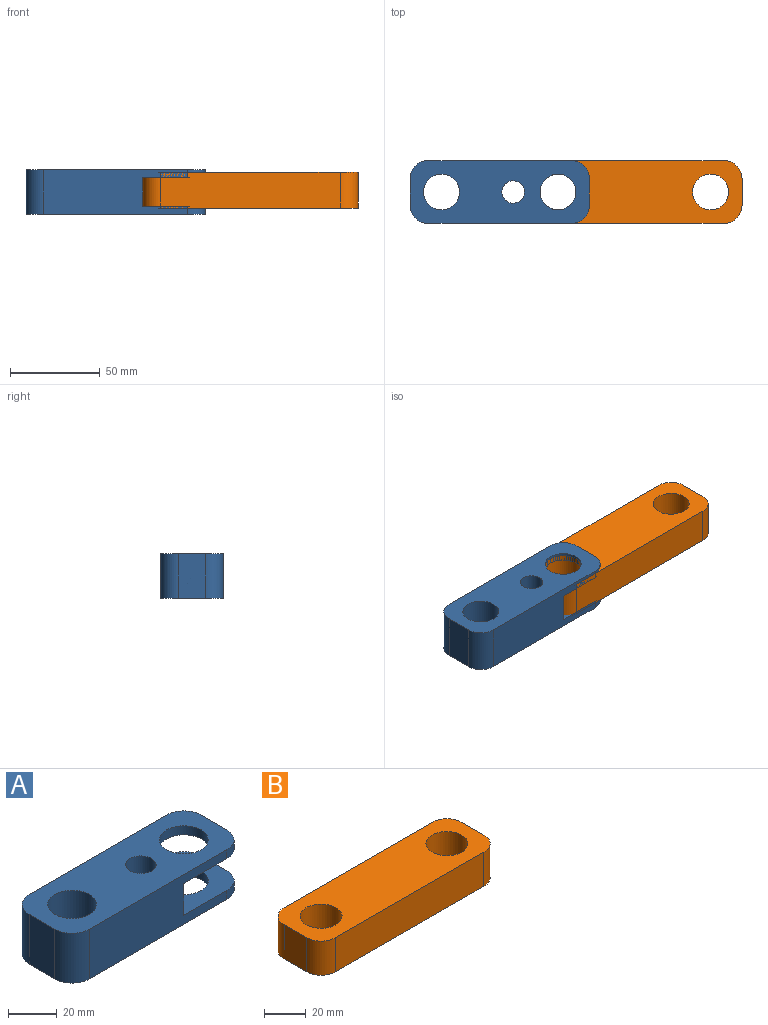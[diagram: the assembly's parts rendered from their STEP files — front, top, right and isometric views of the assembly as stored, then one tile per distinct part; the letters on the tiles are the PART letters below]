
ASSEMBLY  parts=2 mates=1
PART A: 20 faces, bbox 100x35x25 mm
  f0: plane 15x4.5mm, normal (1,0,0), area 67.5mm2, adj f2,f3,f15,f18
  f1: plane 80x25mm, normal (0,-1,0), area 1600mm2, adj f2,f7,f8,f15,f16,f17,f18,f19
  f2: cylinder r=10mm len=10mm, axis (0,0,-1), area 70.7mm2, adj f0,f1,f15,f18
  f3: cylinder r=10mm len=10mm, axis (0,0,-1), area 70.7mm2, adj f0,f4,f15,f18
  f4: plane 80x25mm, normal (0,1,0), area 1600mm2, adj f3,f10,f14,f15,f16,f17,f18,f19
  f5: cylinder r=10mm len=20mm, axis (0,0,-1), area 282.7mm2, adj f15,f18
  f6: plane 25x15mm, normal (-1,0,0), area 375mm2, adj f7,f14,f15,f16
  f7: cylinder r=10mm len=25mm, axis (0,0,-1), area 392.7mm2, adj f1,f6,f15,f16
  f8: cylinder r=10mm len=10mm, axis (0,0,-1), area 70.7mm2, adj f1,f9,f16,f19
  f9: plane 15x4.5mm, normal (1,0,0), area 67.5mm2, adj f8,f10,f16,f19
  f10: cylinder r=10mm len=10mm, axis (0,0,-1), area 70.7mm2, adj f4,f9,f16,f19
  f11: cylinder r=10mm len=25mm, axis (0,0,-1), area 1570.8mm2, adj f15,f16
  f12: cylinder r=10mm len=20mm, axis (0,0,-1), area 282.7mm2, adj f16,f19
  f13: cylinder r=6.25mm len=25mm, axis (0,0,-1), area 981.7mm2, adj f15,f16
  f14: cylinder r=10mm len=25mm, axis (0,0,-1), area 392.7mm2, adj f4,f6,f15,f16
  f15: plane 100x35mm, normal (0,0,1), area 2663.1mm2, adj f0,f1,f2,f3,f4,f5,f6,f7
  f16: plane 100x35mm, normal (0,0,-1), area 2663.1mm2, adj f1,f4,f6,f7,f8,f9,f10,f11
  f17: plane 35x16mm, normal (1,0,0), area 560mm2, adj f1,f4,f18,f19
  f18: plane 35x35mm, normal (0,0,-1), area 867.9mm2, adj f0,f1,f2,f3,f4,f5,f17
  f19: plane 35x35mm, normal (0,0,1), area 867.9mm2, adj f1,f4,f8,f9,f10,f12,f17
PART B: 12 faces, bbox 120x35x20 mm
  f0: plane 20x15mm, normal (-1,0,0), area 300mm2, adj f1,f9,f10,f11
  f1: cylinder r=10mm len=20mm, axis (0,0,-1), area 314.2mm2, adj f0,f2,f10,f11
  f2: plane 100x20mm, normal (0,-1,0), area 2000mm2, adj f1,f3,f10,f11
  f3: cylinder r=10mm len=20mm, axis (0,0,-1), area 314.2mm2, adj f2,f4,f10,f11
  f4: plane 20x15mm, normal (1,0,0), area 300mm2, adj f3,f5,f10,f11
  f5: cylinder r=10mm len=20mm, axis (0,0,-1), area 314.2mm2, adj f4,f6,f10,f11
  f6: plane 100x20mm, normal (0,1,0), area 2000mm2, adj f5,f9,f10,f11
  f7: cylinder r=10mm len=20mm, axis (0,0,-1), area 1256.6mm2, adj f10,f11
  f8: cylinder r=10mm len=20mm, axis (0,0,-1), area 1256.6mm2, adj f10,f11
  f9: cylinder r=10mm len=20mm, axis (0,0,-1), area 314.2mm2, adj f0,f6,f10,f11
  f10: plane 120x35mm, normal (0,0,1), area 3485.8mm2, adj f0,f1,f2,f3,f4,f5,f6,f7
  f11: plane 120x35mm, normal (0,0,-1), area 3485.8mm2, adj f0,f1,f2,f3,f4,f5,f6,f7
PLACE A at identity
PLACE B t=(93.13,0,3.5)mm
MATE slider B.f7 <-> A.f5  axis (0,0,-1) through (37.86,0,23.5)mm
